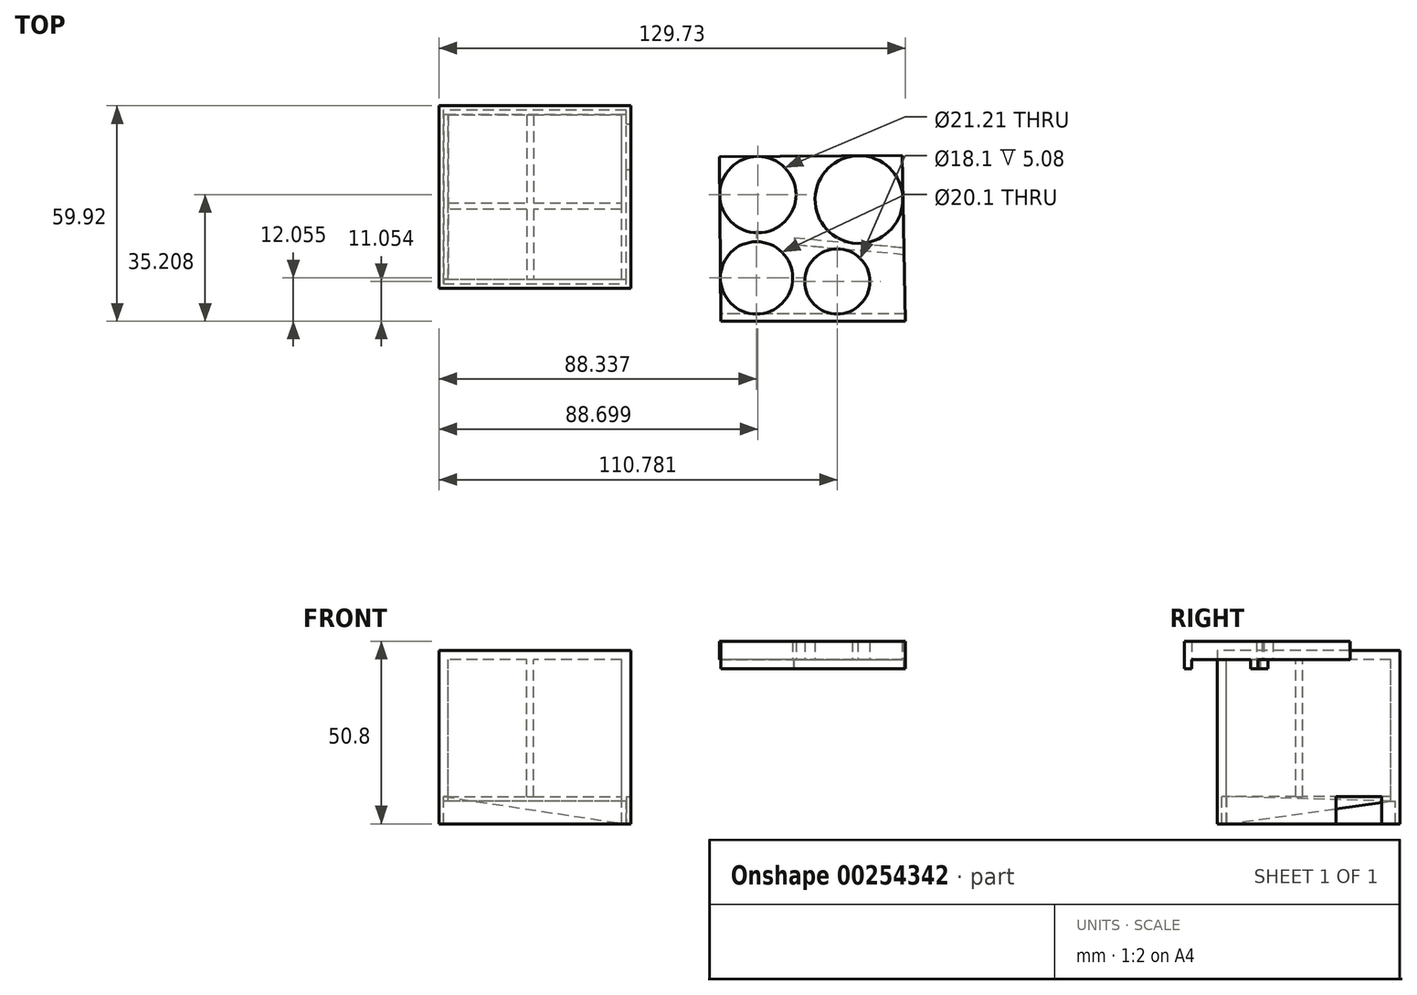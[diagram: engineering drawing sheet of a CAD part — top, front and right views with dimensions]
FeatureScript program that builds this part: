
annotation { "Feature Type Name" : "Feature", "Feature Type Description" : "" }
export const myFeature = defineFeature(function(context is Context, id is Id, definition is map)
    precondition{}
    {
        {
            var Q0;
            Q0=qCreatedBy(makeId("Top.planeOp"),FACE);
            var sketch = newSketch(context, id + "F0", { "sketchPlane" : qUnion([Q0])});
            skLineSegment(sketch, "E0.bottom", {"start": v(-20.12, 31.77) * mm, "end": v(33.22, 31.77) * mm});
            skLineSegment(sketch, "E0.top", {"start": v(-20.12, -19.03) * mm, "end": v(33.22, -19.03) * mm});
            skLineSegment(sketch, "E0.left", {"start": v(-20.12, 31.77) * mm, "end": v(-20.12, -19.03) * mm});
            skLineSegment(sketch, "E0.right", {"start": v(33.22, 31.77) * mm, "end": v(33.22, -19.03) * mm});
            skSolve(sketch);
        }
        {
            var Q0;
            Q0 = qSketchRegion(id + "F0", true);
            extrude(context, id + "F1", {"entities" : qUnion([Q0]), "depth" : 2.54 * mm});
        }
        {
            var Q0;
            Q0=makeQuery(id+"F1.opExtrude","CAP_FACE",FACE,{"disambiguationData":[OSD([sQuery(id+"F0.wireOp",EDGE,"E0.bottom"),sQuery(id+"F0.wireOp",EDGE,"E0.top"),sQuery(id+"F0.wireOp",EDGE,"E0.left"),sQuery(id+"F0.wireOp",EDGE,"E0.right")])],"isStart":true});
            var sketch = newSketch(context, id + "F2", { "sketchPlane" : qUnion([Q0])});
            skLineSegment(sketch, "E1.bottom", {"start": v(-20.12, 19.03) * mm, "end": v(-18.85, 19.03) * mm});
            skLineSegment(sketch, "E1.top", {"start": v(-20.12, -31.77) * mm, "end": v(-18.85, -31.77) * mm});
            skLineSegment(sketch, "E1.left", {"start": v(-20.12, 19.03) * mm, "end": v(-20.12, -31.77) * mm});
            skLineSegment(sketch, "E1.right", {"start": v(-18.85, 17.76) * mm, "end": v(-18.85, -30.5) * mm});
            skLineSegment(sketch, "E2.bottom", {"start": v(33.22, 19.03) * mm, "end": v(31.95, 19.03) * mm});
            skLineSegment(sketch, "E2.top", {"start": v(33.22, -31.77) * mm, "end": v(31.95, -31.77) * mm});
            skLineSegment(sketch, "E2.left", {"start": v(33.22, 19.03) * mm, "end": v(33.22, -31.77) * mm});
            skLineSegment(sketch, "E2.right", {"start": v(31.95, 17.76) * mm, "end": v(31.95, -30.5) * mm});
            skLineSegment(sketch, "E3.bottom", {"start": v(-18.85, 19.03) * mm, "end": v(31.95, 19.03) * mm});
            skLineSegment(sketch, "E3.top", {"start": v(-18.85, 17.76) * mm, "end": v(31.95, 17.76) * mm});
            skLineSegment(sketch, "E4.bottom", {"start": v(-18.85, -31.77) * mm, "end": v(31.95, -31.77) * mm});
            skLineSegment(sketch, "E4.top", {"start": v(-18.85, -30.5) * mm, "end": v(31.95, -30.5) * mm});
            skSolve(sketch);
        }
        {
            var Q0;
            Q0 = qSketchRegion(id + "F2", true);
            extrude(context, id + "F3", {"entities" : qUnion([Q0]), "operationType" : NewBodyOperationType.ADD, "depth" : 45.72 * mm});
        }
        {
            var Q0;
            Q0=makeQuery(id+"F3.opExtrude","CAP_FACE",FACE,{"disambiguationData":[OSD([sQuery(id+"F2.wireOp",EDGE,"E1.bottom"),sQuery(id+"F2.wireOp",EDGE,"E1.top"),sQuery(id+"F2.wireOp",EDGE,"E1.left"),sQuery(id+"F2.wireOp",EDGE,"E1.right"),sQuery(id+"F2.wireOp",EDGE,"E2.bottom"),sQuery(id+"F2.wireOp",EDGE,"E2.top"),sQuery(id+"F2.wireOp",EDGE,"E2.left"),sQuery(id+"F2.wireOp",EDGE,"E2.right"),sQuery(id+"F2.wireOp",EDGE,"E3.bottom"),sQuery(id+"F2.wireOp",EDGE,"E3.top"),sQuery(id+"F2.wireOp",EDGE,"E4.bottom"),sQuery(id+"F2.wireOp",EDGE,"E4.top")])],"isStart":false});
            var sketch = newSketch(context, id + "F4", { "sketchPlane" : qUnion([Q0])});
            skLineSegment(sketch, "E5.bottom", {"start": v(31.95, -13.99) * mm, "end": v(33.22, -13.99) * mm});
            skLineSegment(sketch, "E5.top", {"start": v(31.95, -26.69) * mm, "end": v(33.22, -26.69) * mm});
            skLineSegment(sketch, "E5.left", {"start": v(31.95, -13.99) * mm, "end": v(31.95, -26.69) * mm});
            skLineSegment(sketch, "E5.right", {"start": v(33.22, -13.99) * mm, "end": v(33.22, -26.69) * mm});
            skSolve(sketch);
        }
        {
            var Q0;
            Q0 = qSketchRegion(id + "F4", true);
            extrude(context, id + "F5", {"entities" : qUnion([Q0]), "operationType" : NewBodyOperationType.REMOVE, "oppositeDirection" : true, "depth" : 7.62 * mm});
        }
        {
            var Q0;
            Q0=makeQuery(id+"F3.opExtrude","SWEPT_FACE",FACE,{"disambiguationData":[OSD([sQuery(id+"F2.wireOp",EDGE,"E4.top")])]});
            var sketch = newSketch(context, id + "F6", { "sketchPlane" : qUnion([Q0])});
            skLineSegment(sketch, "E6.bottom", {"start": v(31.95, 0) * mm, "end": v(-18.85, 0) * mm});
            skLineSegment(sketch, "E6.left", {"start": v(31.95, 0) * mm, "end": v(31.95, -39.37) * mm});
            skLineSegment(sketch, "E6.right", {"start": v(-18.85, 0) * mm, "end": v(-18.85, -39.37) * mm});
            skLineSegment(sketch, "E7", {"start": v(31.95, -39.37) * mm, "end": v(-18.85, -39.37) * mm});
            skSolve(sketch);
        }
        {
            var Q0;
            Q0 = qSketchRegion(id + "F6", true);
            extrude(context, id + "F7", {"entities" : qUnion([Q0]), "operationType" : NewBodyOperationType.ADD, "depth" : 1.27 * mm});
        }
        {
            var Q0;
            Q0=makeQuery(id+"F3.opExtrude","SWEPT_FACE",FACE,{"disambiguationData":[OSD([sQuery(id+"F2.wireOp",EDGE,"E3.top")])]});
            var sketch = newSketch(context, id + "F8", { "sketchPlane" : qUnion([Q0])});
            skLineSegment(sketch, "E8.bottom", {"start": v(18.85, 0) * mm, "end": v(-31.95, 0) * mm});
            skLineSegment(sketch, "E8.left", {"start": v(18.85, 0) * mm, "end": v(18.85, -38.1) * mm});
            skLineSegment(sketch, "E8.right", {"start": v(-31.95, 0) * mm, "end": v(-31.95, -45.72) * mm});
            skLineSegment(sketch, "E9", {"start": v(18.85, -38.1) * mm, "end": v(-31.95, -45.72) * mm});
            skSolve(sketch);
        }
        {
            var Q0;
            Q0 = qSketchRegion(id + "F8", true);
            extrude(context, id + "F9", {"entities" : qUnion([Q0]), "operationType" : NewBodyOperationType.ADD, "depth" : 1.27 * mm});
        }
        {
            var Q0;
            Q0=makeQuery(id+"F3.opExtrude","SWEPT_FACE",FACE,{"disambiguationData":[OSD([sQuery(id+"F2.wireOp",EDGE,"E2.right")])]});
            var sketch = newSketch(context, id + "F10", { "sketchPlane" : qUnion([Q0])});
            skLineSegment(sketch, "E10.left", {"start": v(16.5, 0) * mm, "end": v(16.5, -45.72) * mm});
            skLineSegment(sketch, "E10.right", {"start": v(-29.23, 0) * mm, "end": v(-29.23, -39.37) * mm});
            skLineSegment(sketch, "E11", {"start": v(16.5, -45.72) * mm, "end": v(-29.23, -39.37) * mm});
            skLineSegment(sketch, "E12", {"start": v(16.5, 0) * mm, "end": v(-29.23, 0) * mm});
            skSolve(sketch);
        }
        {
            var Q0;
            Q0 = qSketchRegion(id + "F10", true);
            extrude(context, id + "F11", {"entities" : qUnion([Q0]), "operationType" : NewBodyOperationType.ADD, "depth" : 1.27 * mm});
        }
        {
            var Q0;
            Q0=makeQuery(id+"F3.opExtrude","SWEPT_FACE",FACE,{"disambiguationData":[OSD([sQuery(id+"F2.wireOp",EDGE,"E1.right")])]});
            var sketch = newSketch(context, id + "F12", { "sketchPlane" : qUnion([Q0])});
            skLineSegment(sketch, "E13", {"start": v(-16.5, 0) * mm, "end": v(-16.5, -38.1) * mm});
            skLineSegment(sketch, "E14", {"start": v(-16.5, 0) * mm, "end": v(29.23, 0) * mm});
            skLineSegment(sketch, "E15", {"start": v(29.23, 0) * mm, "end": v(29.23, -39.37) * mm});
            skLineSegment(sketch, "E16", {"start": v(29.23, -39.37) * mm, "end": v(-16.5, -38.1) * mm});
            skSolve(sketch);
        }
        {
            var Q0;
            Q0 = qSketchRegion(id + "F12", true);
            extrude(context, id + "F13", {"entities" : qUnion([Q0]), "operationType" : NewBodyOperationType.ADD, "depth" : 1.27 * mm});
        }
        {
            var Q0;
            Q0=makeQuery(id+"F1.opExtrude","CAP_FACE",FACE,{"disambiguationData":[OSD([sQuery(id+"F0.wireOp",EDGE,"E0.bottom"),sQuery(id+"F0.wireOp",EDGE,"E0.top"),sQuery(id+"F0.wireOp",EDGE,"E0.left"),sQuery(id+"F0.wireOp",EDGE,"E0.right")])],"isStart":true});
            var sketch = newSketch(context, id + "F14", { "sketchPlane" : qUnion([Q0])});
            skLineSegment(sketch, "E17", {"start": v(6.18, -29.23) * mm, "end": v(6.18, -4.73) * mm});
            skLineSegment(sketch, "E18", {"start": v(30.68, -2.93) * mm, "end": v(6.18, -2.93) * mm});
            skLineSegment(sketch, "E19", {"start": v(-17.58, -4.73) * mm, "end": v(4.38, -4.73) * mm});
            skLineSegment(sketch, "E20", {"start": v(6.18, 16.5) * mm, "end": v(4.38, 16.5) * mm});
            skLineSegment(sketch, "E21", {"start": v(-17.58, -2.93) * mm, "end": v(-17.58, -4.73) * mm});
            skLineSegment(sketch, "E22", {"start": v(4.38, -29.23) * mm, "end": v(6.18, -29.23) * mm});
            skLineSegment(sketch, "E23", {"start": v(30.68, -29.23) * mm, "end": v(30.68, -2.93) * mm});
            skLineSegment(sketch, "E24", {"start": v(4.38, -29.23) * mm, "end": v(4.38, -4.73) * mm});
            skLineSegment(sketch, "E25.trimOffspring", {"start": v(6.18, -4.73) * mm, "end": v(30.68, -4.73) * mm});
            skLineSegment(sketch, "E26.trimOffspring", {"start": v(6.18, -2.93) * mm, "end": v(6.18, 16.5) * mm});
            skLineSegment(sketch, "E27.trimOffspring", {"start": v(4.38, -2.93) * mm, "end": v(4.38, 16.5) * mm});
            skLineSegment(sketch, "E28.trimOffspring", {"start": v(4.38, -2.93) * mm, "end": v(-17.58, -2.93) * mm});
            skSolve(sketch);
        }
        {
            var Q0;
            Q0 = qSketchRegion(id + "F14", true);
            extrude(context, id + "F15", {"entities" : qUnion([Q0]), "operationType" : NewBodyOperationType.ADD, "depth" : 38.1 * mm});
        }
        {
            var Q0;
            Q0=qCreatedBy(makeId("Top.planeOp"),FACE);
            var sketch = newSketch(context, id + "F16", { "sketchPlane" : qUnion([Q0])});
            skLineSegment(sketch, "E29.bottom", {"start": v(58.24, -28.15) * mm, "end": v(109.61, -28.15) * mm});
            skLineSegment(sketch, "E29.top", {"start": v(57.87, 17.6) * mm, "end": v(108.67, 18) * mm});
            skLineSegment(sketch, "E29.left", {"start": v(58.24, -28.15) * mm, "end": v(57.87, 17.6) * mm});
            skLineSegment(sketch, "E29.right", {"start": v(109.61, -28.15) * mm, "end": v(108.67, 18) * mm});
            skCircle(sketch, "E30", {"center": v(68.22, -16.1) * mm, "radius": 10.05 * mm});
            skCircle(sketch, "E31", {"center": v(90.66, -17.1) * mm, "radius": 9.05 * mm});
            skCircle(sketch, "E32", {"center": v(68.58, 7.06) * mm, "radius": 10.6 * mm});
            skCircle(sketch, "E33", {"center": v(96.7, 5.69) * mm, "radius": 12.2 * mm});
            skSolve(sketch);
        }
        {
            var Q0;
            Q0 = qSketchRegion(id + "F16", true);
            extrude(context, id + "F17", {"entities" : qUnion([Q0]), "depth" : 5.08 * mm});
        }
        {
            var Q0;
            Q0=makeQuery(id+"F17.opExtrude","CAP_FACE",FACE,{"disambiguationData":[OSD([sQuery(id+"F16.wireOp",EDGE,"E29.bottom"),sQuery(id+"F16.wireOp",EDGE,"E29.top"),sQuery(id+"F16.wireOp",EDGE,"E29.left"),sQuery(id+"F16.wireOp",EDGE,"E29.right"),sQuery(id+"F16.wireOp",EDGE,"E30"),sQuery(id+"F16.wireOp",EDGE,"E31"),sQuery(id+"F16.wireOp",EDGE,"E32"),sQuery(id+"F16.wireOp",EDGE,"E33")])],"isStart":false});
            var sketch = newSketch(context, id + "F18", { "sketchPlane" : qUnion([Q0])});
            skLineSegment(sketch, "E34.bottom", {"start": v(58.24, -28.15) * mm, "end": v(109.61, -28.15) * mm});
            skLineSegment(sketch, "E34.left", {"start": v(58.24, -28.15) * mm, "end": v(58.23, -26.15) * mm});
            skLineSegment(sketch, "E34.right", {"start": v(109.61, -28.15) * mm, "end": v(109.57, -26.15) * mm});
            skLineSegment(sketch, "E35", {"start": v(109.57, -26.15) * mm, "end": v(58.23, -26.15) * mm});
            skLineSegment(sketch, "E36", {"start": v(109.24, -9.67) * mm, "end": v(78.64, -6.94) * mm});
            skLineSegment(sketch, "E37", {"start": v(78.72, -4.94) * mm, "end": v(109.2, -7.65) * mm});
            skLineSegment(sketch, "E38.trimOffspring", {"start": v(109.24, -9.67) * mm, "end": v(109.2, -7.65) * mm});
            skLineSegment(sketch, "E39", {"start": v(78.72, -4.94) * mm, "end": v(78.64, -6.94) * mm});
            skSolve(sketch);
        }
        {
            var Q0;
            Q0 = qSketchRegion(id + "F18", true);
            extrude(context, id + "F19", {"entities" : qUnion([Q0]), "operationType" : NewBodyOperationType.ADD, "oppositeDirection" : true, "depth" : 7.62 * mm});
        }
    });
